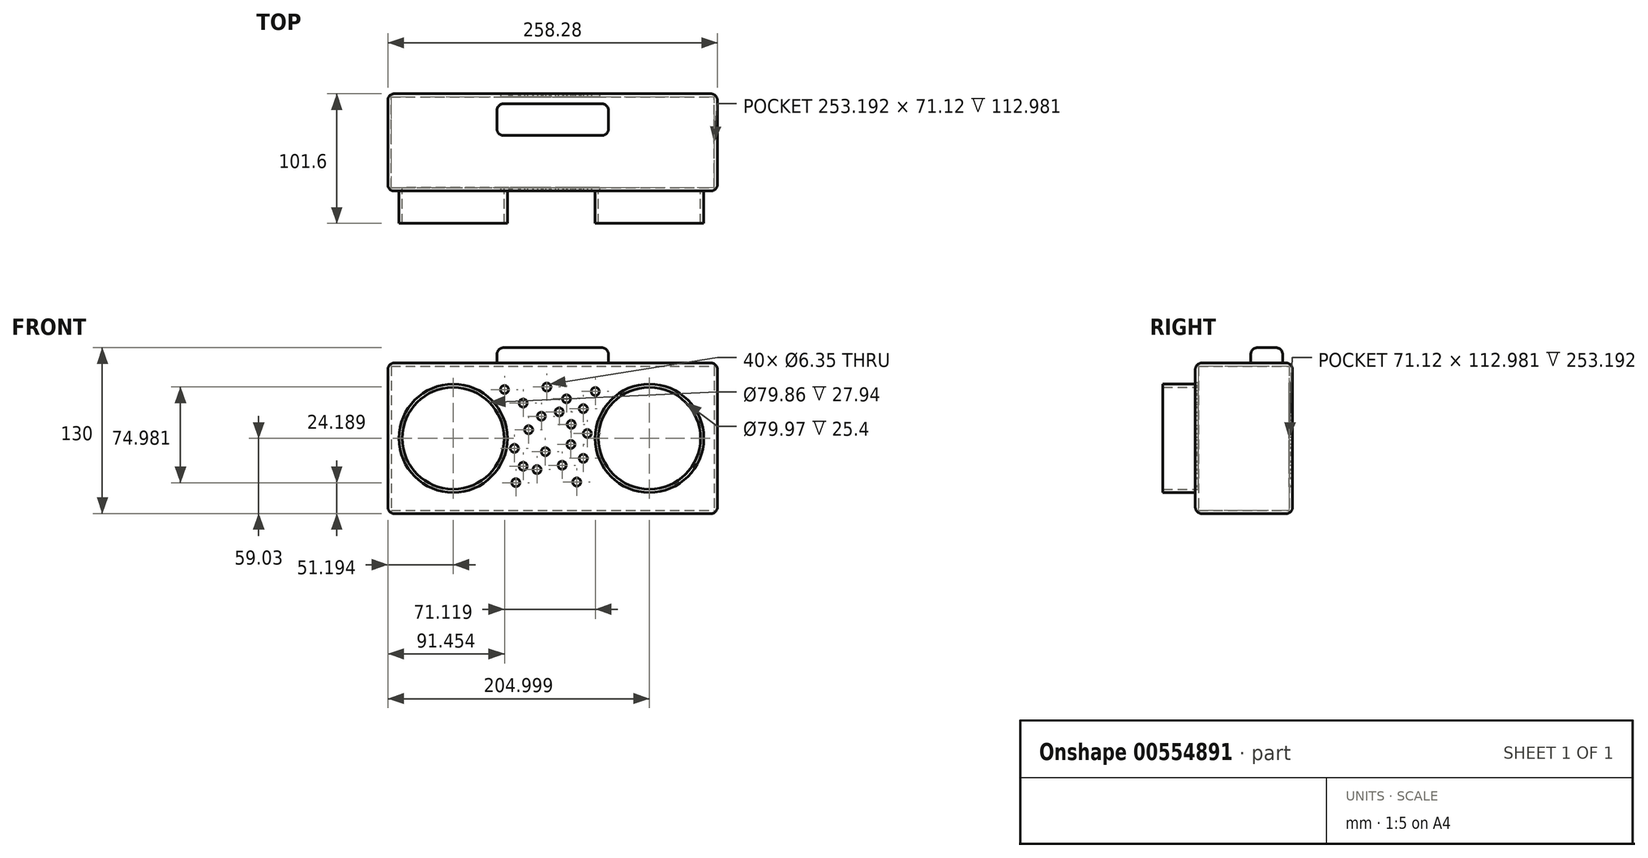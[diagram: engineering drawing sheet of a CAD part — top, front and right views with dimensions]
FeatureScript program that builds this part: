
annotation { "Feature Type Name" : "Feature", "Feature Type Description" : "" }
export const myFeature = defineFeature(function(context is Context, id is Id, definition is map)
    precondition{}
    {
        {
            var Q0;
            Q0=qCreatedBy(makeId("Front.planeOp"),FACE);
            var sketch = newSketch(context, id + "F0", { "sketchPlane" : qUnion([Q0])});
            skLineSegment(sketch, "E0.bottom", {"start": v(-129.14, 59.03) * mm, "end": v(129.14, 59.03) * mm});
            skLineSegment(sketch, "E0.top", {"start": v(-129.14, -59.03) * mm, "end": v(129.14, -59.03) * mm});
            skLineSegment(sketch, "E0.left", {"start": v(-129.14, 59.03) * mm, "end": v(-129.14, -59.03) * mm});
            skLineSegment(sketch, "E0.right", {"start": v(129.14, 59.03) * mm, "end": v(129.14, -59.03) * mm});
            skPoint(sketch, "E0.middle", {"position": v(0, 0) * mm});
            skSolve(sketch);
        }
        {
            var Q0;
            Q0 = qSketchRegion(id + "F0", true);
            extrude(context, id + "F1", {"entities" : qUnion([Q0]), "depth" : 76.2 * mm, "offsetDistance" : 25.4 * mm});
        }
        {
            var Q0;
            Q0=makeQuery(id+"F1.opExtrude","CAP_FACE",FACE,{"disambiguationData":[OSD([sQuery(id+"F0.wireOp",EDGE,"E0.bottom"),sQuery(id+"F0.wireOp",EDGE,"E0.top"),sQuery(id+"F0.wireOp",EDGE,"E0.left"),sQuery(id+"F0.wireOp",EDGE,"E0.right")])],"isStart":false});
            var sketch = newSketch(context, id + "F2", { "sketchPlane" : qUnion([Q0])});
            skCircle(sketch, "E1", {"center": v(-77.95, 0) * mm, "radius": 42.47 * mm});
            skCircle(sketch, "E2", {"center": v(74.86, 0) * mm, "radius": 43 * mm});
            skSolve(sketch);
        }
        {
            var Q0;
            Q0=makeQuery(id+"F2.imprint","IMPRINT",FACE,{"disambiguationData":[TD([[makeQuery(id+"F2.imprint","IMPRINT",EDGE,{"derivedFrom":sQuery(id+"F2.wireOp",EDGE,"E1")}),1.0]])]});
            extrude(context, id + "F3", {"entities" : qUnion([Q0]), "operationType" : NewBodyOperationType.ADD, "depth" : 25.4 * mm, "offsetDistance" : 25.4 * mm});
        }
        {
            var Q0;
            Q0=makeQuery(id+"F3.opExtrude","CAP_FACE",FACE,{"disambiguationData":[OSD([sQuery(id+"F2.wireOp",EDGE,"E1")])],"isStart":false});
            shell(context, id + "F4", {"entities" : qUnion([Q0]), "thickness" : 2.54 * mm});
        }
        {
            var Q0;
            Q0=makeQuery(id+"F1.opExtrude","CAP_FACE",FACE,{"disambiguationData":[OSD([sQuery(id+"F0.wireOp",EDGE,"E0.bottom"),sQuery(id+"F0.wireOp",EDGE,"E0.top"),sQuery(id+"F0.wireOp",EDGE,"E0.left"),sQuery(id+"F0.wireOp",EDGE,"E0.right")])],"isStart":false});
            var sketch = newSketch(context, id + "F5", { "sketchPlane" : qUnion([Q0])});
            skCircle(sketch, "E3", {"center": v(75.86, 0) * mm, "radius": 42.52 * mm});
            skSolve(sketch);
        }
        {
            var Q0;
            Q0=makeQuery(id+"F5.imprint","IMPRINT",FACE,{"disambiguationData":[TD([[makeQuery(id+"F5.imprint","IMPRINT",EDGE,{"derivedFrom":sQuery(id+"F5.wireOp",EDGE,"E3")}),1.0]])]});
            extrude(context, id + "F6", {"entities" : qUnion([Q0]), "operationType" : NewBodyOperationType.ADD, "depth" : 25.4 * mm, "offsetDistance" : 25.4 * mm});
        }
        {
            var Q0;
            Q0=makeQuery(id+"F6.opExtrude","CAP_FACE",FACE,{"disambiguationData":[OSD([sQuery(id+"F5.wireOp",EDGE,"E3")])],"isStart":false});
            shell(context, id + "F7", {"entities" : qUnion([Q0]), "thickness" : 2.54 * mm});
        }
        {
            var Q0;
            Q0=makeQuery(id+"F1.opExtrude","SWEPT_FACE",FACE,{"disambiguationData":[OSD([sQuery(id+"F0.wireOp",EDGE,"E0.bottom")])]});
            var sketch = newSketch(context, id + "F8", { "sketchPlane" : qUnion([Q0])});
            skLineSegment(sketch, "E4.bottom", {"start": v(43.66, -7.84) * mm, "end": v(-43.66, -7.84) * mm});
            skLineSegment(sketch, "E4.top", {"start": v(43.66, -32.72) * mm, "end": v(-43.66, -32.72) * mm});
            skLineSegment(sketch, "E4.left", {"start": v(43.66, -7.84) * mm, "end": v(43.66, -32.72) * mm});
            skLineSegment(sketch, "E4.right", {"start": v(-43.66, -7.84) * mm, "end": v(-43.66, -32.72) * mm});
            skPoint(sketch, "E4.middle", {"position": v(0, -20.28) * mm});
            skSolve(sketch);
        }
        {
            var Q0;
            Q0=makeQuery(id+"F8.imprint","IMPRINT",FACE,{"disambiguationData":[TD([[makeQuery(id+"F8.imprint","IMPRINT",EDGE,{"derivedFrom":sQuery(id+"F8.wireOp",EDGE,"E4.bottom")}),1.0]])]});
            extrude(context, id + "F9", {"entities" : qUnion([Q0]), "operationType" : NewBodyOperationType.ADD, "depth" : 11.94 * mm, "offsetDistance" : 25.4 * mm});
        }
        {
            var Q0;
            Q0=makeQuery(id+"F1.opExtrude","SWEPT_EDGE",EDGE,{"disambiguationData":[OSD([sQuery(id+"F0.wireOp",EDGE,"E0.bottom"),sQuery(id+"F0.wireOp",EDGE,"E0.left")])]});
            var Q1;
            Q1=makeQuery(id+"F1.opExtrude","SWEPT_EDGE",EDGE,{"disambiguationData":[OSD([sQuery(id+"F0.wireOp",EDGE,"E0.top"),sQuery(id+"F0.wireOp",EDGE,"E0.left")])]});
            var Q2;
            Q2=makeQuery(id+"F1.opExtrude","SWEPT_EDGE",EDGE,{"disambiguationData":[OSD([sQuery(id+"F0.wireOp",EDGE,"E0.bottom"),sQuery(id+"F0.wireOp",EDGE,"E0.right")])]});
            var Q3;
            Q3=makeQuery(id+"F1.opExtrude","SWEPT_EDGE",EDGE,{"disambiguationData":[OSD([sQuery(id+"F0.wireOp",EDGE,"E0.top"),sQuery(id+"F0.wireOp",EDGE,"E0.right")])]});
            var Q4;
            Q4=makeQuery(id+"F1.opExtrude","CAP_EDGE",EDGE,{"disambiguationData":[OSD([sQuery(id+"F0.wireOp",EDGE,"E0.right")])],"isStart":false});
            var Q5;
            Q5=makeQuery(id+"F1.opExtrude","CAP_EDGE",EDGE,{"disambiguationData":[OSD([sQuery(id+"F0.wireOp",EDGE,"E0.bottom")])],"isStart":false});
            var Q6;
            Q6=makeQuery(id+"F1.opExtrude","CAP_EDGE",EDGE,{"disambiguationData":[OSD([sQuery(id+"F0.wireOp",EDGE,"E0.top")])],"isStart":false});
            var Q7;
            Q7=makeQuery(id+"F1.opExtrude","CAP_EDGE",EDGE,{"disambiguationData":[OSD([sQuery(id+"F0.wireOp",EDGE,"E0.right")])],"isStart":true});
            var Q8;
            Q8=makeQuery(id+"F1.opExtrude","CAP_EDGE",EDGE,{"disambiguationData":[OSD([sQuery(id+"F0.wireOp",EDGE,"E0.bottom")])],"isStart":true});
            var Q9;
            Q9=makeQuery(id+"F1.opExtrude","CAP_EDGE",EDGE,{"disambiguationData":[OSD([sQuery(id+"F0.wireOp",EDGE,"E0.top")])],"isStart":true});
            var Q10;
            Q10=makeQuery(id+"F1.opExtrude","CAP_EDGE",EDGE,{"disambiguationData":[OSD([sQuery(id+"F0.wireOp",EDGE,"E0.left")])],"isStart":true});
            var Q11;
            Q11=makeQuery(id+"F1.opExtrude","CAP_EDGE",EDGE,{"disambiguationData":[OSD([sQuery(id+"F0.wireOp",EDGE,"E0.left")])],"isStart":false});
            var Q12;
            Q12=makeQuery(id+"F9.opExtrude","CAP_EDGE",EDGE,{"disambiguationData":[OSD([sQuery(id+"F8.wireOp",EDGE,"E4.right")])],"isStart":false});
            var Q13;
            Q13=makeQuery(id+"F9.opExtrude","CAP_EDGE",EDGE,{"disambiguationData":[OSD([sQuery(id+"F8.wireOp",EDGE,"E4.top")])],"isStart":false});
            var Q14;
            Q14=makeQuery(id+"F9.opExtrude","CAP_EDGE",EDGE,{"disambiguationData":[OSD([sQuery(id+"F8.wireOp",EDGE,"E4.bottom")])],"isStart":false});
            var Q15;
            Q15=makeQuery(id+"F9.opExtrude","CAP_EDGE",EDGE,{"disambiguationData":[OSD([sQuery(id+"F8.wireOp",EDGE,"E4.left")])],"isStart":false});
            var Q16;
            Q16=makeQuery(id+"F9.opExtrude","SWEPT_EDGE",EDGE,{"disambiguationData":[OSD([sQuery(id+"F8.wireOp",EDGE,"E4.top"),sQuery(id+"F8.wireOp",EDGE,"E4.right")])]});
            var Q17;
            Q17=makeQuery(id+"F9.opExtrude","SWEPT_EDGE",EDGE,{"disambiguationData":[OSD([sQuery(id+"F8.wireOp",EDGE,"E4.bottom"),sQuery(id+"F8.wireOp",EDGE,"E4.right")])]});
            var Q18;
            Q18=makeQuery(id+"F9.opExtrude","SWEPT_EDGE",EDGE,{"disambiguationData":[OSD([sQuery(id+"F8.wireOp",EDGE,"E4.top"),sQuery(id+"F8.wireOp",EDGE,"E4.left")])]});
            var Q19;
            Q19=makeQuery(id+"F9.opExtrude","SWEPT_EDGE",EDGE,{"disambiguationData":[OSD([sQuery(id+"F8.wireOp",EDGE,"E4.bottom"),sQuery(id+"F8.wireOp",EDGE,"E4.left")])]});
            fillet(context, id + "F10", {"entities" : qUnion([Q0, Q1, Q2, Q3, Q4, Q5, Q6, Q7, Q8, Q9, Q10, Q11, Q12, Q13, Q14, Q15, Q16, Q17, Q18, Q19]), "radius" : 5.08 * mm, "tangentPropagation" : true, "allowEdgeOverflow" : false});
        }
        {
            var Q0;
            Q0=makeQuery(id+"F1.opExtrude","CAP_FACE",FACE,{"disambiguationData":[OSD([sQuery(id+"F0.wireOp",EDGE,"E0.bottom"),sQuery(id+"F0.wireOp",EDGE,"E0.top"),sQuery(id+"F0.wireOp",EDGE,"E0.left"),sQuery(id+"F0.wireOp",EDGE,"E0.right")])],"isStart":false});
            var sketch = newSketch(context, id + "F11", { "sketchPlane" : qUnion([Q0])});
            skPoint(sketch, "E5", {"position": v(-33.12, 31.01) * mm});
            skPoint(sketch, "E6", {"position": v(-13.98, 24.12) * mm});
            skPoint(sketch, "E7", {"position": v(-4.55, 40.14) * mm});
            skPoint(sketch, "E8", {"position": v(17.72, 30.38) * mm});
            skPoint(sketch, "E9", {"position": v(18, 13.48) * mm});
            skPoint(sketch, "E10", {"position": v(31.72, 21.2) * mm});
            skPoint(sketch, "E11", {"position": v(-25.69, 4.66) * mm});
            skPoint(sketch, "E12", {"position": v(-21.7, -19.68) * mm});
            skPoint(sketch, "E13", {"position": v(-7.7, -10.53) * mm});
            skPoint(sketch, "E14", {"position": v(17.44, -19.73) * mm});
            skPoint(sketch, "E15", {"position": v(8.87, -4.83) * mm});
            skPoint(sketch, "E16", {"position": v(31.72, -34.35) * mm});
            skPoint(sketch, "E17", {"position": v(10.01, -34.6) * mm});
            skPoint(sketch, "E18", {"position": v(-13.98, -37.15) * mm});
            skPoint(sketch, "E19", {"position": v(-38.54, -32.25) * mm});
            skSolve(sketch);
        }
        {
            var Q0;
            Q0=sQuery(id+"F11.wireOp",VERTEX,"E7");
            var Q1;
            Q1=makeQuery(id+"F1.opExtrude","SWEPT_BODY",BODY,{"disambiguationData":[OSD([sQuery(id+"F0.wireOp",EDGE,"E0.bottom"),sQuery(id+"F0.wireOp",EDGE,"E0.top"),sQuery(id+"F0.wireOp",EDGE,"E0.left"),sQuery(id+"F0.wireOp",EDGE,"E0.right")])]});
            hole(context, id + "F12", {"style" : HoleStyle.SIMPLE, "endStyle" : HoleEndStyle.THROUGH, "holeDiameter" : 6.35 * mm, "isTappedThrough" : true, "tappedDepth" : 12.7 * mm, "tapClearance" : 3, "locations" : qUnion([Q0]), "scope" : qUnion([Q1])});
        }
        {
            var Q0;
            Q0=makeQuery(id+"F1.opExtrude","CAP_FACE",FACE,{"disambiguationData":[OSD([sQuery(id+"F0.wireOp",EDGE,"E0.bottom"),sQuery(id+"F0.wireOp",EDGE,"E0.top"),sQuery(id+"F0.wireOp",EDGE,"E0.left"),sQuery(id+"F0.wireOp",EDGE,"E0.right")])],"isStart":false});
            var sketch = newSketch(context, id + "F13", { "sketchPlane" : qUnion([Q0])});
            skPoint(sketch, "E20", {"position": v(-23.12, 27.57) * mm});
            skPoint(sketch, "E21", {"position": v(-8.84, 17.24) * mm});
            skPoint(sketch, "E22", {"position": v(-37.69, 38.18) * mm});
            skPoint(sketch, "E23", {"position": v(10.87, 30.96) * mm});
            skPoint(sketch, "E24", {"position": v(5.16, 20.66) * mm});
            skPoint(sketch, "E25", {"position": v(24, 23.21) * mm});
            skPoint(sketch, "E26", {"position": v(-18.83, 6.66) * mm});
            skPoint(sketch, "E27", {"position": v(-29.97, -7.93) * mm});
            skPoint(sketch, "E28", {"position": v(-5.7, -10.53) * mm});
            skPoint(sketch, "E29", {"position": v(-23.12, -21.96) * mm});
            skPoint(sketch, "E30", {"position": v(-12.27, -24.56) * mm});
            skPoint(sketch, "E31", {"position": v(7.44, -21.15) * mm});
            skPoint(sketch, "E32", {"position": v(14.3, -4.83) * mm});
            skPoint(sketch, "E33", {"position": v(14.58, 10.91) * mm});
            skPoint(sketch, "E34", {"position": v(27.15, 3.74) * mm});
            skPoint(sketch, "E35", {"position": v(24, -15.73) * mm});
            skPoint(sketch, "E36", {"position": v(33.43, 36.66) * mm});
            skPoint(sketch, "E37", {"position": v(-28.83, -34.84) * mm});
            skPoint(sketch, "E38", {"position": v(18.87, -34.33) * mm});
            skSolve(sketch);
        }
        {
            var Q0;
            Q0=sQuery(id+"F13.wireOp",VERTEX,"E22");
            var Q1;
            Q1=sQuery(id+"F13.wireOp",VERTEX,"E20");
            var Q2;
            Q2=sQuery(id+"F13.wireOp",VERTEX,"E23");
            var Q3;
            Q3=sQuery(id+"F13.wireOp",VERTEX,"E36");
            var Q4;
            Q4=sQuery(id+"F13.wireOp",VERTEX,"E25");
            var Q5;
            Q5=sQuery(id+"F13.wireOp",VERTEX,"E21");
            var Q6;
            Q6=sQuery(id+"F13.wireOp",VERTEX,"E24");
            var Q7;
            Q7=sQuery(id+"F13.wireOp",VERTEX,"E26");
            var Q8;
            Q8=sQuery(id+"F13.wireOp",VERTEX,"E33");
            var Q9;
            Q9=sQuery(id+"F13.wireOp",VERTEX,"E34");
            var Q10;
            Q10=sQuery(id+"F13.wireOp",VERTEX,"E35");
            var Q11;
            Q11=sQuery(id+"F13.wireOp",VERTEX,"E32");
            var Q12;
            Q12=sQuery(id+"F13.wireOp",VERTEX,"E27");
            var Q13;
            Q13=sQuery(id+"F13.wireOp",VERTEX,"E28");
            var Q14;
            Q14=sQuery(id+"F13.wireOp",VERTEX,"E29");
            var Q15;
            Q15=sQuery(id+"F13.wireOp",VERTEX,"E30");
            var Q16;
            Q16=sQuery(id+"F13.wireOp",VERTEX,"E37");
            var Q17;
            Q17=sQuery(id+"F13.wireOp",VERTEX,"E31");
            var Q18;
            Q18=sQuery(id+"F13.wireOp",VERTEX,"E38");
            var Q19;
            Q19=makeQuery(id+"F1.opExtrude","SWEPT_BODY",BODY,{"disambiguationData":[OSD([sQuery(id+"F0.wireOp",EDGE,"E0.bottom"),sQuery(id+"F0.wireOp",EDGE,"E0.top"),sQuery(id+"F0.wireOp",EDGE,"E0.left"),sQuery(id+"F0.wireOp",EDGE,"E0.right")])]});
            hole(context, id + "F14", {"style" : HoleStyle.SIMPLE, "endStyle" : HoleEndStyle.THROUGH, "holeDiameter" : 6.35 * mm, "isTappedThrough" : true, "tappedDepth" : 12.7 * mm, "tapClearance" : 3, "locations" : qUnion([Q0, Q1, Q2, Q3, Q4, Q5, Q6, Q7, Q8, Q9, Q10, Q11, Q12, Q13, Q14, Q15, Q16, Q17, Q18]), "scope" : qUnion([Q19])});
        }
    });
